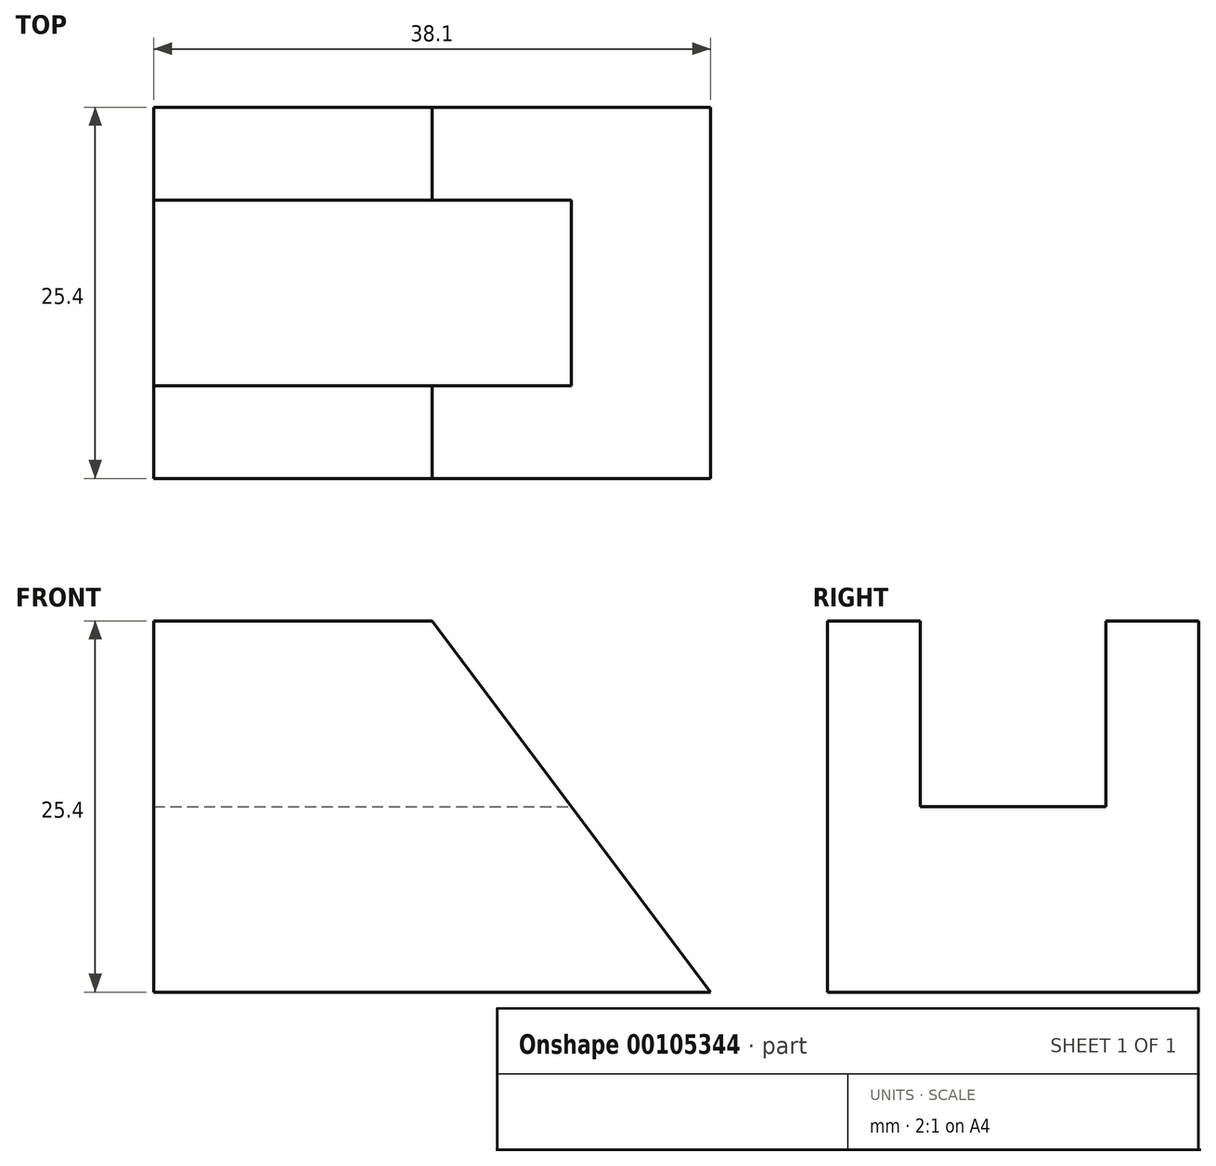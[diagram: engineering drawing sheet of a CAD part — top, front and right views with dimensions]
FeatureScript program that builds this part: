
annotation { "Feature Type Name" : "Feature", "Feature Type Description" : "" }
export const myFeature = defineFeature(function(context is Context, id is Id, definition is map)
    precondition{}
    {
        {
            var Q0;
            Q0=qCreatedBy(makeId("Front.planeOp"),FACE);
            var sketch = newSketch(context, id + "F0", { "sketchPlane" : qUnion([Q0])});
            skLineSegment(sketch, "E0.bottom", {"start": v(0, 0) * mm, "end": v(38.1, 0) * mm});
            skLineSegment(sketch, "E0.top", {"start": v(0, 25.4) * mm, "end": v(38.1, 25.4) * mm});
            skLineSegment(sketch, "E0.left", {"start": v(0, 0) * mm, "end": v(0, 25.4) * mm});
            skLineSegment(sketch, "E0.right", {"start": v(38.1, 0) * mm, "end": v(38.1, 25.4) * mm});
            skSolve(sketch);
        }
        {
            var Q0;
            Q0 = qSketchRegion(id + "F0", true);
            extrude(context, id + "F1", {"entities" : qUnion([Q0]), "endBound" : BoundingType.SYMMETRIC, "depth" : 25.4 * mm});
        }
        {
            var Q0;
            Q0=qCreatedBy(makeId("Front.planeOp"),FACE);
            var sketch = newSketch(context, id + "F2", { "sketchPlane" : qUnion([Q0])});
            skLineSegment(sketch, "E1", {"start": v(19.05, 25.4) * mm, "end": v(38.1, 0) * mm});
            skLineSegment(sketch, "E2", {"start": v(38.1, 0) * mm, "end": v(38.1, 25.4) * mm});
            skLineSegment(sketch, "E3", {"start": v(38.1, 25.4) * mm, "end": v(19.05, 25.4) * mm});
            skSolve(sketch);
        }
        {
            var Q0;
            Q0 = qSketchRegion(id + "F2", true);
            extrude(context, id + "F3", {"entities" : qUnion([Q0]), "operationType" : NewBodyOperationType.REMOVE, "endBound" : BoundingType.SYMMETRIC, "oppositeDirection" : true, "depth" : 127 * mm});
        }
        {
            var Q0;
            Q0=qCreatedBy(makeId("Right.planeOp"),FACE);
            var sketch = newSketch(context, id + "F4", { "sketchPlane" : qUnion([Q0])});
            skLineSegment(sketch, "E4.bottom", {"start": v(6.35, 25.4) * mm, "end": v(-6.35, 25.4) * mm});
            skLineSegment(sketch, "E4.top", {"start": v(6.35, 12.7) * mm, "end": v(-6.35, 12.7) * mm});
            skLineSegment(sketch, "E4.left", {"start": v(6.35, 25.4) * mm, "end": v(6.35, 12.7) * mm});
            skLineSegment(sketch, "E4.right", {"start": v(-6.35, 25.4) * mm, "end": v(-6.35, 12.7) * mm});
            skSolve(sketch);
        }
        {
            var Q0;
            Q0 = qSketchRegion(id + "F4", true);
            extrude(context, id + "F5", {"entities" : qUnion([Q0]), "operationType" : NewBodyOperationType.REMOVE, "endBound" : BoundingType.SYMMETRIC, "oppositeDirection" : true, "depth" : 101.6 * mm});
        }
    });
